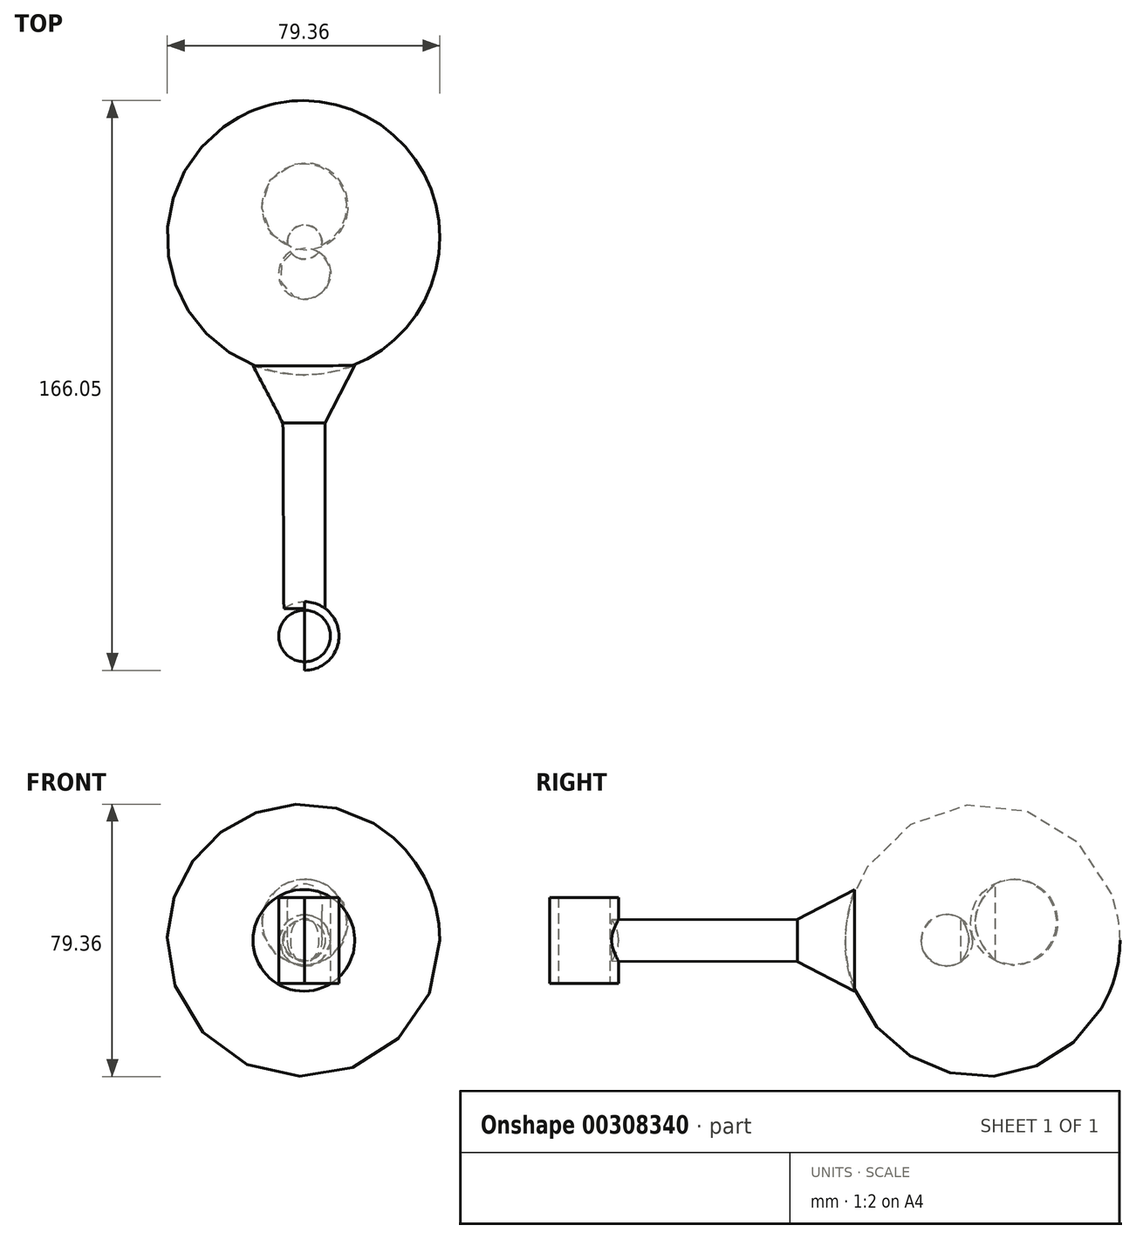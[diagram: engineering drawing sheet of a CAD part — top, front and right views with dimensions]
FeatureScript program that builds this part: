
annotation { "Feature Type Name" : "Feature", "Feature Type Description" : "" }
export const myFeature = defineFeature(function(context is Context, id is Id, definition is map)
    precondition{}
    {
        {
            var Q0;
            Q0=qCreatedBy(makeId("Top.planeOp"),FACE);
            var sketch = newSketch(context, id + "F0", { "sketchPlane" : qUnion([Q0])});
            skArc(sketch, "E0", {"start": v(0, -83.98) * mm, "mid": v(9.87, -75.6) * mm, "end": v(3.2, -64.5) * mm});
            skArc(sketch, "E1", {"start": v(0, -81.48) * mm, "mid": v(7.5, -73.96) * mm, "end": v(-0.04, -66.48) * mm});
            skArc(sketch, "E2", {"start": v(-0.22, 2.08) * mm, "mid": v(40, 42.18) * mm, "end": v(-0.42, 82.07) * mm});
            skArc(sketch, "E3", {"start": v(-0.23, 5.15) * mm, "mid": v(38.5, 43.75) * mm, "end": v(-0.42, 82.15) * mm});
            skLineSegment(sketch, "E4", {"start": v(-0.42, 82.07) * mm, "end": v(0, -83.98) * mm});
            skArc(sketch, "E5.MirrorCS", {"start": v(0, -81.48) * mm, "mid": v(-7.55, -74) * mm, "end": v(-0.04, -66.48) * mm});
            skArc(sketch, "E6.MirrorCS", {"start": v(0, -83.98) * mm, "mid": v(-10.05, -74) * mm, "end": v(-0.05, -63.98) * mm});
            skArc(sketch, "E7.trimOffspring", {"start": v(9.38, -70.5) * mm, "mid": v(5.7, -65.76) * mm, "end": v(-0.05, -63.98) * mm});
            skPoint(sketch, "E8.oppositeSnap0", {"position": v(7.5, -73.96) * mm});
            skPoint(sketch, "E9.orphan", {"position": v(-4.97, 0) * mm});
            skPoint(sketch, "E10.orphan", {"position": v(-7.55, -74) * mm});
            skLineSegment(sketch, "E11", {"start": v(14.58, 4.83) * mm, "end": v(5.96, -11.9) * mm});
            skLineSegment(sketch, "E12", {"start": v(5.96, -11.9) * mm, "end": v(5.96, -65.95) * mm});
            skPoint(sketch, "E8.right.end.orphan", {"position": v(10, -73.96) * mm});
            skSolve(sketch);
        }
        {
            var Q0;
            {var subQ0=sQuery(id+"F0.wireOp",EDGE,"E4");var subQ1=sQuery(id+"F0.wireOp",EDGE,"E2");var subQ2=makeQuery(id+"F0.imprint","INTERSECT",VERTEX,{"disambiguationData":[OD(0.0)],"derivedFrom":[subQ1,subQ0]});Q0=makeQuery(id+"F0.imprint","IMPRINT",FACE,{"disambiguationData":[TD([[makeQuery(id+"F0.imprint","IMPRINT",EDGE,{"disambiguationData":[TD([[subQ2,-1.0]])],"derivedFrom":subQ1}),1.0]])]});}
            var Q1;
            {var subQ7=sQuery(id+"F0.wireOp",EDGE,"E11");Q1=makeQuery(id+"F0.imprint","IMPRINT",FACE,{"disambiguationData":[TD([[makeQuery(id+"F0.imprint","IMPRINT",EDGE,{"derivedFrom":subQ7}),-1.0]])]});}
            var Q2;
            Q2=sQuery(id+"F0.wireOp",EDGE,"E4");
            revolve(context, id + "F1", {"entities" : qUnion([Q0, Q1]), "axis" : qUnion([Q2]), "revolveType" : RevolveType.FULL});
        }
        {
            var Q0;
            {var subQ0=sQuery(id+"F0.wireOp",EDGE,"E1");Q0=makeQuery(id+"F0.imprint","IMPRINT",FACE,{"disambiguationData":[TD([[makeQuery(id+"F0.imprint","IMPRINT",EDGE,{"derivedFrom":subQ0}),-1.0]])]});}
            extrude(context, id + "F2", {"entities" : qUnion([Q0]), "operationType" : NewBodyOperationType.ADD, "endBound" : BoundingType.SYMMETRIC, "depth" : 25 * mm});
        }
        {
            var Q0;
            {var subQ3=sQuery(id+"F0.wireOp",EDGE,"E5.MirrorCS");Q0=makeQuery(id+"F0.imprint","IMPRINT",FACE,{"disambiguationData":[TD([[makeQuery(id+"F0.imprint","IMPRINT",EDGE,{"derivedFrom":subQ3}),1.0]])]});}
            extrude(context, id + "F3", {"entities" : qUnion([Q0]), "operationType" : NewBodyOperationType.ADD, "endBound" : BoundingType.SYMMETRIC, "depth" : 25 * mm});
        }
        {
            var Q0;
            Q0=qCreatedBy(makeId("Right.planeOp"),FACE);
            var sketch = newSketch(context, id + "F4", { "sketchPlane" : qUnion([Q0])});
            skCircle(sketch, "E13", {"center": v(38.7, 18.3) * mm, "radius": 5 * mm});
            skCircle(sketch, "E14", {"center": v(46.13, -13.44) * mm, "radius": 5 * mm});
            skSolve(sketch);
        }
        {
            var Q0;
            Q0 = qSketchRegion(id + "F4", true);
            extrude(context, id + "F5", {"entities" : qUnion([Q0]), "operationType" : NewBodyOperationType.REMOVE, "endBound" : BoundingType.SYMMETRIC, "depth" : 100 * mm});
        }
        {
            var Q0;
            Q0 = qSketchRegion(id + "F4", true);
            extrude(context, id + "F6", {"entities" : qUnion([Q0]), "operationType" : NewBodyOperationType.REMOVE, "endBound" : BoundingType.SYMMETRIC, "oppositeDirection" : true, "depth" : 25 * mm});
        }
        {
            var Q0;
            Q0=makeQuery(id+"F4.imprint","IMPRINT",FACE,{"disambiguationData":[TD([[makeQuery(id+"F4.imprint","IMPRINT",EDGE,{"derivedFrom":sQuery(id+"F4.wireOp",EDGE,"E14")}),1.0]])]});
            extrude(context, id + "F7", {"entities" : qUnion([Q0]), "operationType" : NewBodyOperationType.REMOVE, "oppositeDirection" : true, "depth" : 100 * mm});
        }
        {
            var Q0;
            Q0=qCreatedBy(makeId("Right.planeOp"),FACE);
            var sketch = newSketch(context, id + "F8", { "sketchPlane" : qUnion([Q0])});
            skArc(sketch, "E15", {"start": v(51.05, -7.17) * mm, "mid": v(63.55, 5.17) * mm, "end": v(51.38, 17.83) * mm});
            skArc(sketch, "E16", {"start": v(31.77, -7.5) * mm, "mid": v(39.27, 0.1) * mm, "end": v(31.57, 7.5) * mm});
            skLineSegment(sketch, "E17", {"start": v(31.57, 7.5) * mm, "end": v(31.77, -7.5) * mm});
            skLineSegment(sketch, "E18", {"start": v(51.38, 17.83) * mm, "end": v(51.05, -7.17) * mm});
            skSolve(sketch);
        }
        {
            var Q0;
            Q0=makeQuery(id+"F8.imprint","IMPRINT",FACE,{"disambiguationData":[TD([[makeQuery(id+"F8.imprint","IMPRINT",EDGE,{"derivedFrom":sQuery(id+"F8.wireOp",EDGE,"E16")}),1.0]])]});
            var Q1;
            Q1=sQuery(id+"F8.wireOp",EDGE,"E17");
            revolve(context, id + "F9", {"entities" : qUnion([Q0]), "axis" : qUnion([Q1]), "revolveType" : RevolveType.FULL});
        }
        {
            var Q0;
            Q0=makeQuery(id+"F8.imprint","IMPRINT",FACE,{"disambiguationData":[TD([[makeQuery(id+"F8.imprint","IMPRINT",EDGE,{"derivedFrom":sQuery(id+"F8.wireOp",EDGE,"E15")}),1.0]])]});
            var Q1;
            Q1=sQuery(id+"F8.wireOp",EDGE,"E18");
            revolve(context, id + "F10", {"entities" : qUnion([Q0]), "axis" : qUnion([Q1]), "revolveType" : RevolveType.FULL});
        }
        {
            var Q0;
            Q0=qCreatedBy(makeId("Top.planeOp"),FACE);
            var sketch = newSketch(context, id + "F11", { "sketchPlane" : qUnion([Q0])});
            skCircle(sketch, "E19", {"center": v(0, 40.81) * mm, "radius": 5 * mm});
            skSolve(sketch);
        }
        {
            var Q0;
            Q0 = qSketchRegion(id + "F11", true);
            extrude(context, id + "F12", {"entities" : qUnion([Q0]), "operationType" : NewBodyOperationType.REMOVE, "endBound" : BoundingType.SYMMETRIC, "oppositeDirection" : true, "depth" : 100 * mm});
        }
    });
